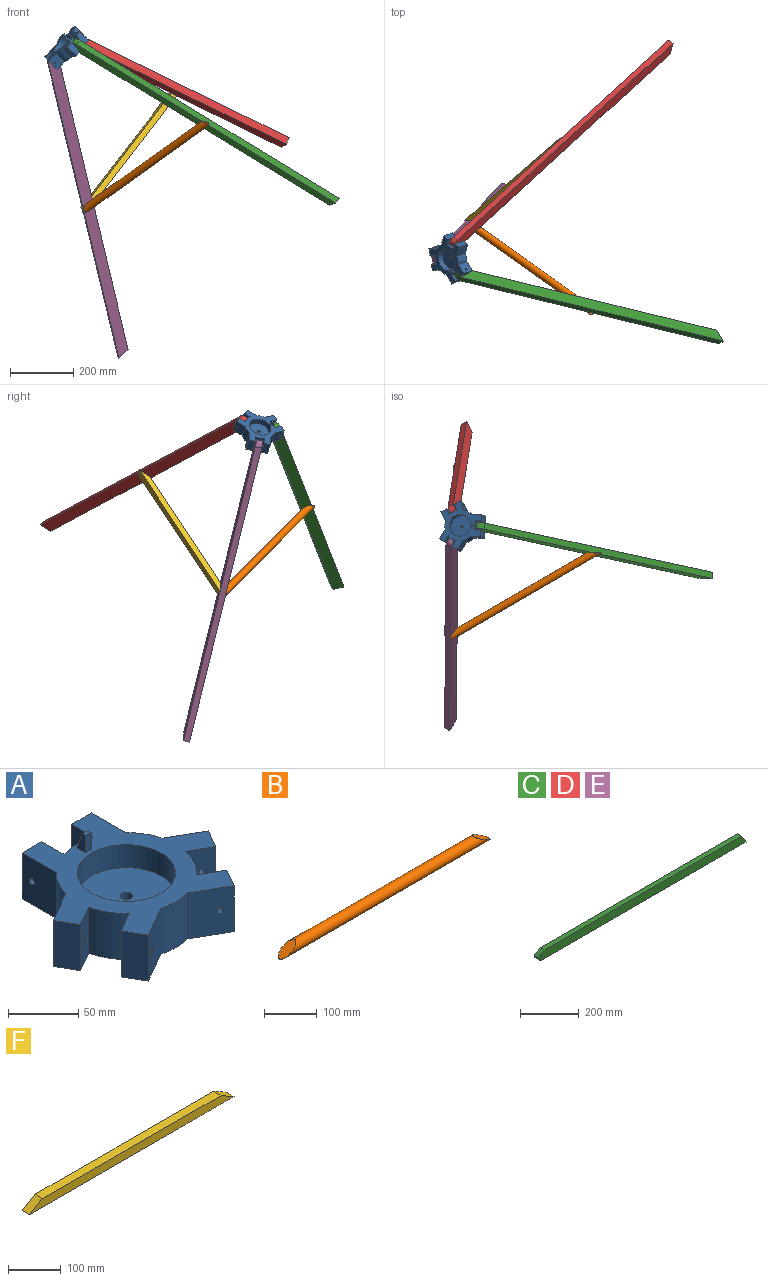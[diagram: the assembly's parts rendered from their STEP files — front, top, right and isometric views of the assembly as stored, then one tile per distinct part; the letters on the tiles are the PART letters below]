
ASSEMBLY  parts=6 mates=5
PART A: 41 faces, bbox 156.2x135.3x55 mm
  f0: cylinder r=50mm len=40mm, axis (0,0,-1), area 1218.8mm2, adj f7,f8,f25,f26
  f1: cylinder r=50mm len=40mm, axis (0,0,-1), area 1087.2mm2, adj f7,f8,f22,f23
  f2: cylinder r=50mm len=40mm, axis (0,0,-1), area 1218.8mm2, adj f7,f8,f18,f20
  f3: cylinder r=50mm len=40mm, axis (0,0,-1), area 1087.2mm2, adj f7,f8,f16,f19
  f4: cylinder r=50mm len=40mm, axis (0,0,-1), area 1218.8mm2, adj f7,f8,f13,f14
  f5: cylinder r=50mm len=40mm, axis (0,0,-1), area 1087.2mm2, adj f7,f8,f11,f28
  f6: cylinder r=35mm len=70mm, axis (0,0,-1), area 4398.2mm2, adj f7,f9
  f7: plane 156.24x135.31mm, normal (0,0,1), area 7224.4mm2, adj f0,f1,f2,f3,f4,f5,f6,f11
  f8: plane 156.24x135.31mm, normal (0,0,-1), area 11060mm2, adj f0,f1,f2,f3,f4,f5,f10,f11
  f9: plane 70x70mm, normal (0,0,1), area 3787.6mm2, adj f6,f10
  f10: cylinder r=4.4mm len=20mm, axis (0,0,-1), area 552.9mm2, adj f8,f9
  f11: plane 40x34.29mm, normal (1,0,0), area 1352.1mm2, adj f5,f7,f8,f12,f34
  f12: plane 40x20mm, normal (0,1,0), area 800mm2, adj f7,f8,f11,f13
  f13: plane 40x22.3mm, normal (-1,0,0), area 872.5mm2, adj f4,f7,f8,f12,f34
  f14: plane 40x22.3mm, normal (1,0,0), area 872.5mm2, adj f4,f7,f8,f15,f33
  f15: plane 40x20mm, normal (0,1,0), area 800mm2, adj f7,f8,f14,f16
  f16: plane 40x34.29mm, normal (-1,0,0), area 1352.1mm2, adj f3,f7,f8,f15,f33
  f17: plane 40x17.32mm, normal (-0.87,-0.5,0), area 800mm2, adj f7,f8,f18,f19
  f18: plane 40x19.32mm, normal (0.5,-0.87,0), area 872.5mm2, adj f2,f7,f8,f17,f32
  f19: plane 40x29.7mm, normal (-0.5,0.87,0), area 1352.1mm2, adj f3,f7,f8,f17,f32
  f20: plane 40x19.32mm, normal (-0.5,0.87,0), area 872.5mm2, adj f2,f7,f8,f21,f31
  f21: plane 40x17.32mm, normal (-0.87,-0.5,0), area 800mm2, adj f7,f8,f20,f22
  f22: plane 40x29.7mm, normal (0.5,-0.87,0), area 1352.1mm2, adj f1,f7,f8,f21,f31
  f23: plane 40x29.7mm, normal (-0.5,-0.87,0), area 1352.1mm2, adj f1,f7,f8,f24,f30
  f24: plane 40x17.32mm, normal (0.87,-0.5,0), area 800mm2, adj f7,f8,f23,f25
  f25: plane 40x19.32mm, normal (0.5,0.87,0), area 872.5mm2, adj f0,f7,f8,f24,f30
  f26: plane 40x19.32mm, normal (-0.5,-0.87,0), area 872.5mm2, adj f0,f7,f8,f27,f29
  f27: plane 40x17.32mm, normal (0.87,-0.5,0), area 800mm2, adj f7,f8,f26,f28
  f28: plane 40x29.7mm, normal (0.5,0.87,0), area 1352.1mm2, adj f5,f7,f8,f27,f29
  f29: cylinder r=2.5mm len=19.82mm, axis (0.5,0.87,0), area 314.2mm2, adj f26,f28
  f30: cylinder r=2.5mm len=19.82mm, axis (0.5,0.87,0), area 314.2mm2, adj f23,f25
  f31: cylinder r=2.5mm len=19.82mm, axis (0.5,-0.87,0), area 314.2mm2, adj f20,f22
  f32: cylinder r=2.5mm len=19.82mm, axis (0.5,-0.87,0), area 314.2mm2, adj f18,f19
  f33: cylinder r=2.5mm len=20mm, axis (-1,0,0), area 314.2mm2, adj f14,f16
  f34: cylinder r=2.5mm len=20mm, axis (-1,0,0), area 314.2mm2, adj f11,f13
  f35: plane 15x8mm, normal (1,0,0), area 85.7mm2, adj f7,f36,f38,f39,f40
  f36: plane 6x1.26mm, normal (0,1,0), area 7.6mm2, adj f7,f35,f37,f40
  f37: plane 15x8mm, normal (-1,0,0), area 85.7mm2, adj f7,f36,f38,f39,f40
  f38: plane 15x6mm, normal (0,-1,0), area 90mm2, adj f7,f35,f37,f39
  f39: plane 6x3mm, normal (0,0,1), area 18mm2, adj f35,f37,f38,f40
  f40: plane 13.74x6mm, normal (0,0.94,0.34), area 87.7mm2, adj f35,f36,f37,f39
PART B: 3 faces, bbox 569.3x32.7x32.7 mm
  f0: cylinder r=12mm len=560.53mm, axis (-1,0,0), area 39107mm2, adj f1,f2
  f1: plane 41.57x24mm, normal (0.5,0,0.87), area 904.8mm2, adj f0
  f2: plane 50.31x32.74mm, normal (-0.5,0,0.87), area 904.8mm2, adj f0
PART C: 9 faces, bbox 999.8x20x35 mm
  f0: plane 949.79x20mm, normal (0,0,1), area 18995.9mm2, adj f1,f2,f6,f7
  f1: plane 999.84x35mm, normal (0,-1,0), area 34281.2mm2, adj f0,f3,f4,f5,f6,f7,f8
  f2: plane 999.84x35mm, normal (0,1,0), area 34281.2mm2, adj f0,f3,f4,f5,f6,f7,f8
  f3: cylinder r=20mm len=20mm, axis (0,-1,0), area 5.9mm2, adj f1,f2,f5,f6
  f4: plane 980x20mm, normal (0,0,-1), area 19600mm2, adj f1,f2,f5,f7
  f5: cylinder r=20mm len=20mm, axis (0,1,0), area 578.2mm2, adj f1,f2,f3,f4
  f6: plane 29.8x20mm, normal (-0.5,0,0.87), area 688.3mm2, adj f0,f1,f2,f3
  f7: plane 35x20.21mm, normal (0.87,0,0.5), area 808.3mm2, adj f0,f1,f2,f4
  f8: cylinder r=2.5mm len=20mm, axis (0,-1,0), area 314.2mm2, adj f1,f2
PART D: same geometry as C
PART E: same geometry as C
PART F: 6 faces, bbox 547.3x20x20 mm
  f0: plane 547.28x20mm, normal (0,0,-1), area 10945.6mm2, adj f1,f3,f4,f5
  f1: plane 547.28x20mm, normal (0,1,0), area 10252.8mm2, adj f0,f2,f4,f5
  f2: plane 478x20mm, normal (0,0,1), area 9560mm2, adj f1,f3,f4,f5
  f3: plane 547.28x20mm, normal (0,-1,0), area 10252.8mm2, adj f0,f2,f4,f5
  f4: plane 34.64x20mm, normal (0.5,0,0.87), area 800mm2, adj f0,f1,f2,f3
  f5: plane 34.64x20mm, normal (-0.5,0,0.87), area 800mm2, adj f0,f1,f2,f3
PLACE A rot(axis=(0.41,0.02,-0.91),148deg) t=(-385.13,-806.29,60.47)mm
PLACE B rot(axis=(-0.78,-0.15,-0.61),76.2deg) t=(-362.94,-1004.27,-163.5)mm
PLACE C rot(axis=(-0.95,0.25,0.2),124.3deg) t=(118.19,-905.77,-49.95)mm
PLACE D rot(axis=(0.91,0.41,-0.06),143.2deg) t=(-156.18,-368.99,-119.84)mm
PLACE E rot(axis=(0.05,0.98,0.2),77deg) t=(-325.27,-843.56,-460.29)mm
PLACE F rot(axis=(0.09,0.72,-0.69),123.7deg) t=(-398.62,-524.32,-115.3)mm
MATE revolute A.f29 <-> E.f8  axis (-0.16,0.97,0.2) through (-439.34,-824.66,29.65)mm
MATE revolute A.f31 <-> D.f8  axis (0.7,-0.5,0.5) through (-396.12,-754.28,97.87)mm
MATE revolute D.f1 <-> F.f5  axis (-0.7,0.5,-0.5) through (-55.79,-448.88,-64.3)mm
MATE revolute B.f2 <-> E.f1  axis (-0.16,0.97,0.2) through (-330.75,-707.53,-428.47)mm
MATE revolute A.f14 <-> C.f8  axis (-0.54,-0.47,-0.7) through (-361.08,-854.27,95.18)mm
